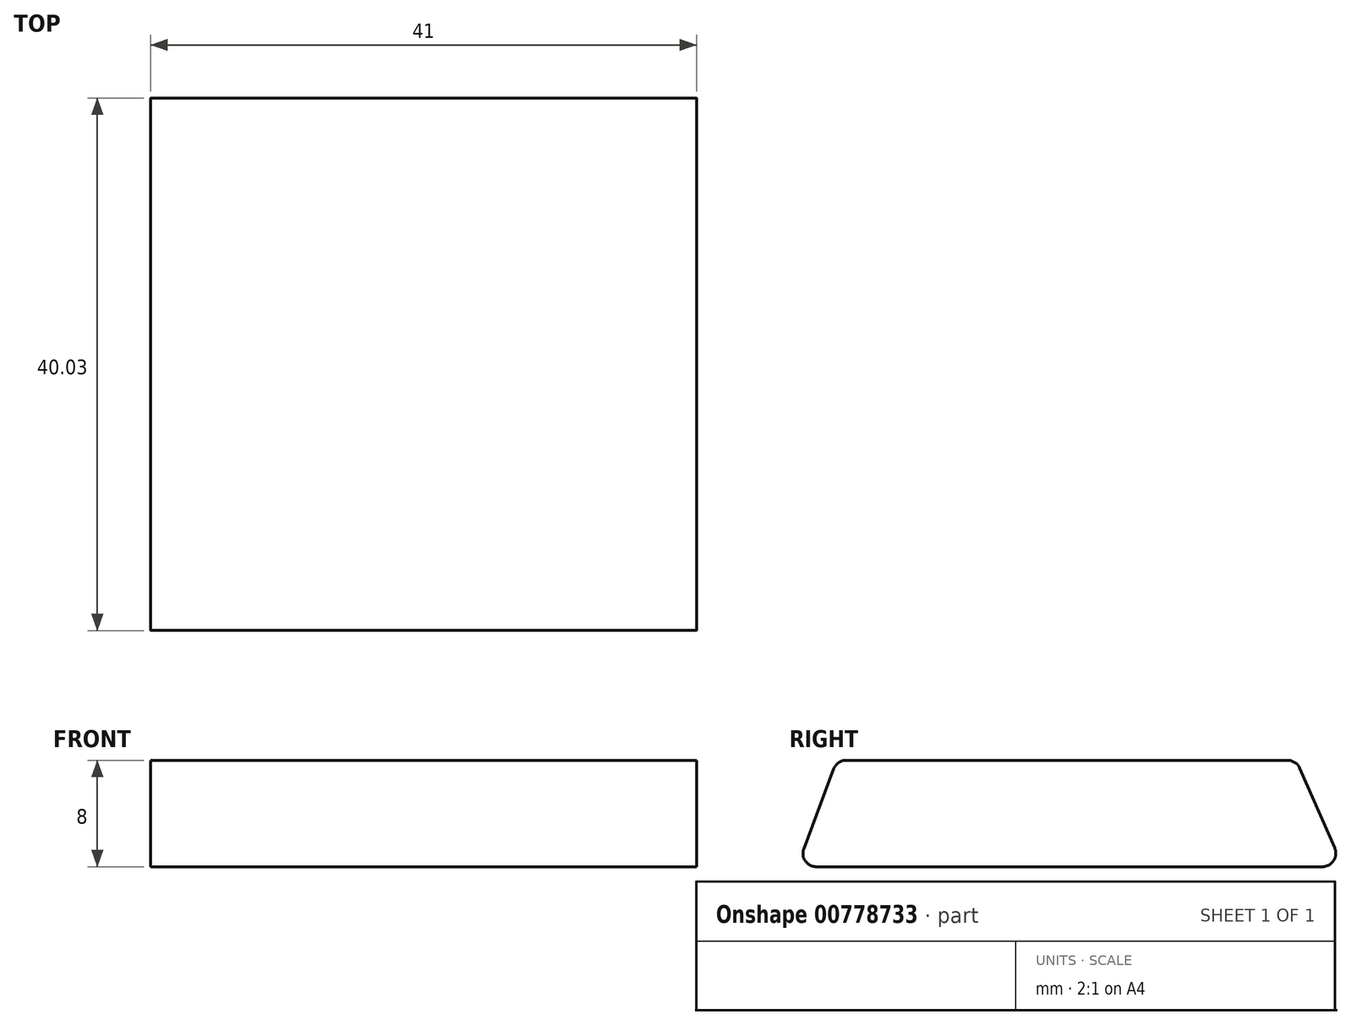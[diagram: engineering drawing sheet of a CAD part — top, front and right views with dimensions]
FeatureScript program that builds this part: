
annotation { "Feature Type Name" : "Feature", "Feature Type Description" : "" }
export const myFeature = defineFeature(function(context is Context, id is Id, definition is map)
    precondition{}
    {
        {
            var Q0;
            Q0=qCreatedBy(makeId("Right.planeOp"),FACE);
            var sketch = newSketch(context, id + "F0", { "sketchPlane" : qUnion([Q0])});
            skLineSegment(sketch, "E0", {"start": v(-20.5, 0) * mm, "end": v(20.5, 0) * mm});
            skPoint(sketch, "E1", {"position": v(0, 0) * mm});
            skLineSegment(sketch, "E2", {"start": v(17, 0) * mm, "end": v(17, 10.5) * mm, "construction": true});
            skLineSegment(sketch, "E3", {"start": v(-17.5, 0) * mm, "end": v(-17.5, 11.1) * mm, "construction": true});
            skLineSegment(sketch, "E4", {"start": v(0, 0) * mm, "end": v(0, 8) * mm, "construction": true});
            skLineSegment(sketch, "E5", {"start": v(17, 8) * mm, "end": v(-17.5, 8) * mm});
            skLineSegment(sketch, "E6", {"start": v(-20.5, 0) * mm, "end": v(-17.5, 8) * mm});
            skLineSegment(sketch, "E7", {"start": v(20.5, 0) * mm, "end": v(17, 8) * mm});
            skSolve(sketch);
        }
        {
            var Q0;
            Q0=makeQuery(id+"F0.imprint","IMPRINT",FACE,{"disambiguationData":[TD([[makeQuery(id+"F0.imprint","IMPRINT",EDGE,{"derivedFrom":sQuery(id+"F0.wireOp",EDGE,"E0")}),1.0]])]});
            extrude(context, id + "F1", {"entities" : qUnion([Q0]), "depth" : 41 * mm, "offsetDistance" : 25 * mm, "symmetric" : true});
        }
        {
            var Q0;
            Q0=makeQuery(id+"F1.opExtrude","SWEPT_EDGE",EDGE,{"disambiguationData":[OSD([sQuery(id+"F0.wireOp",EDGE,"E0"),sQuery(id+"F0.wireOp",EDGE,"E6")])]});
            var Q1;
            Q1=makeQuery(id+"F1.opExtrude","SWEPT_EDGE",EDGE,{"disambiguationData":[OSD([sQuery(id+"F0.wireOp",EDGE,"E5"),sQuery(id+"F0.wireOp",EDGE,"E6")])]});
            var Q2;
            Q2=makeQuery(id+"F1.opExtrude","SWEPT_EDGE",EDGE,{"disambiguationData":[OSD([sQuery(id+"F0.wireOp",EDGE,"E5"),sQuery(id+"F0.wireOp",EDGE,"E7")])]});
            var Q3;
            Q3=makeQuery(id+"F1.opExtrude","SWEPT_EDGE",EDGE,{"disambiguationData":[OSD([sQuery(id+"F0.wireOp",EDGE,"E0"),sQuery(id+"F0.wireOp",EDGE,"E7")])]});
            fillet(context, id + "F2", {"entities" : qUnion([Q0, Q1, Q2, Q3]), "radius" : 1 * mm, "tangentPropagation" : true, "allowEdgeOverflow" : false});
        }
    });
